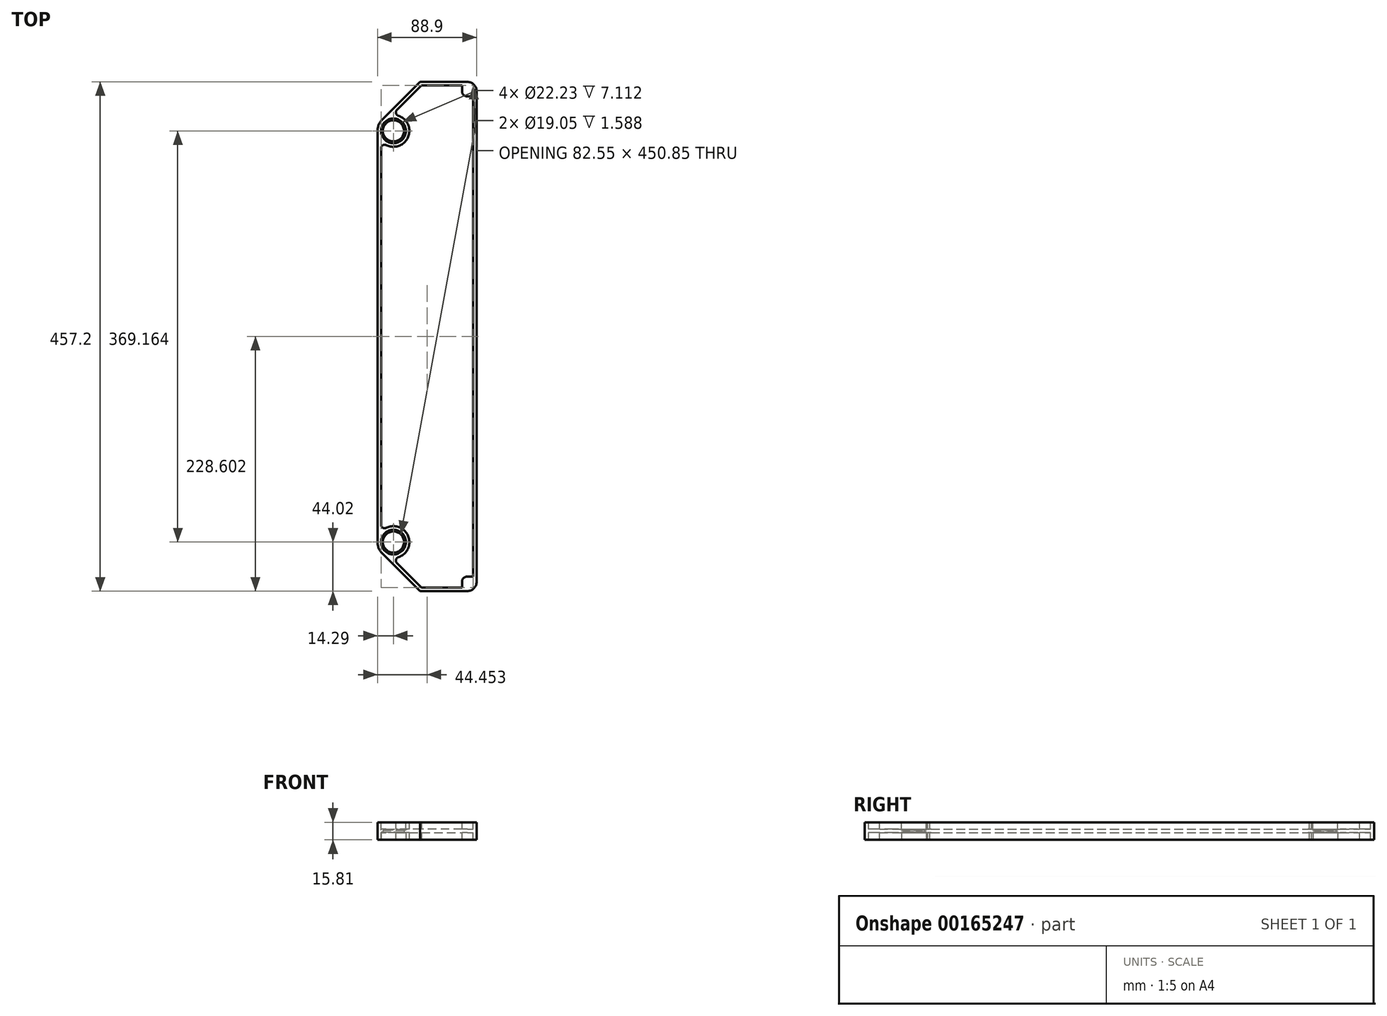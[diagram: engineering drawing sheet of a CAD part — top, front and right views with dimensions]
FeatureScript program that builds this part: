
annotation { "Feature Type Name" : "Feature", "Feature Type Description" : "" }
export const myFeature = defineFeature(function(context is Context, id is Id, definition is map)
    precondition{}
    {
        {
            var Q0;
            Q0=qCreatedBy(makeId("Top.planeOp"),FACE);
            var sketch = newSketch(context, id + "F0", { "sketchPlane" : qUnion([Q0])});
            skCircle(sketch, "E0", {"center": v(0, 0) * mm, "radius": 9.53 * mm});
            skArc(sketch, "E1", {"start": v(-14.29, 0) * mm, "mid": v(-13.2, -5.47) * mm, "end": v(-10.1, -10.1) * mm});
            skLineSegment(sketch, "E2", {"start": v(-14.29, 0) * mm, "end": v(-14.29, 369.16) * mm});
            skArc(sketch, "E3", {"start": v(-10.1, 379.27) * mm, "mid": v(-13.2, 374.63) * mm, "end": v(-14.29, 369.16) * mm});
            skCircle(sketch, "E4", {"center": v(0, 369.16) * mm, "radius": 9.53 * mm});
            skLineSegment(sketch, "E5", {"start": v(-10.1, -10.1) * mm, "end": v(23.81, -44.02) * mm});
            skLineSegment(sketch, "E6", {"start": v(23.81, -44.02) * mm, "end": v(74.61, -44.02) * mm});
            skLineSegment(sketch, "E7", {"start": v(74.61, -44.02) * mm, "end": v(74.61, 413.18) * mm});
            skLineSegment(sketch, "E8", {"start": v(74.61, 413.18) * mm, "end": v(23.81, 413.18) * mm});
            skLineSegment(sketch, "E9", {"start": v(23.81, 413.18) * mm, "end": v(-10.1, 379.27) * mm});
            skLineSegment(sketch, "E10", {"start": v(-14.29, 184.58) * mm, "end": v(23.81, 184.58) * mm, "construction": true});
            skLineSegment(sketch, "E11", {"start": v(23.81, -44.02) * mm, "end": v(23.81, 413.18) * mm, "construction": true});
            skSolve(sketch);
        }
        {
            var Q0;
            Q0=qSketchRegion(id+"F0",true);
            extrude(context, id + "F1", {"entities" : qUnion([Q0]), "depth" : 15.8 * mm});
        }
        {
            var Q0;
            Q0=makeQuery(id+"F1.opExtrude","CAP_FACE",FACE,{"disambiguationData":[OSD([sQuery(id+"F0.wireOp",EDGE,"E0"),sQuery(id+"F0.wireOp",EDGE,"E1"),sQuery(id+"F0.wireOp",EDGE,"E2"),sQuery(id+"F0.wireOp",EDGE,"E3"),sQuery(id+"F0.wireOp",EDGE,"E4"),sQuery(id+"F0.wireOp",EDGE,"E5"),sQuery(id+"F0.wireOp",EDGE,"E6"),sQuery(id+"F0.wireOp",EDGE,"E7"),sQuery(id+"F0.wireOp",EDGE,"E8"),sQuery(id+"F0.wireOp",EDGE,"E9")])],"isStart":false});
            var sketch = newSketch(context, id + "F2", { "sketchPlane" : qUnion([Q0])});
            skCircle(sketch, "E12", {"center": v(0, 369.16) * mm, "radius": 11.11 * mm});
            skCircle(sketch, "E13", {"center": v(0, 0) * mm, "radius": 11.11 * mm});
            skSolve(sketch);
        }
        {
            var Q0;
            Q0=qSketchRegion(id+"F2",true);
            extrude(context, id + "F3", {"entities" : qUnion([Q0]), "operationType" : NewBodyOperationType.REMOVE, "oppositeDirection" : true, "depth" : 7.11 * mm});
        }
        {
            var Q0;
            Q0=makeQuery(id+"F1.opExtrude","CAP_FACE",FACE,{"disambiguationData":[OSD([sQuery(id+"F0.wireOp",EDGE,"E0"),sQuery(id+"F0.wireOp",EDGE,"E1"),sQuery(id+"F0.wireOp",EDGE,"E2"),sQuery(id+"F0.wireOp",EDGE,"E3"),sQuery(id+"F0.wireOp",EDGE,"E4"),sQuery(id+"F0.wireOp",EDGE,"E5"),sQuery(id+"F0.wireOp",EDGE,"E6"),sQuery(id+"F0.wireOp",EDGE,"E7"),sQuery(id+"F0.wireOp",EDGE,"E8"),sQuery(id+"F0.wireOp",EDGE,"E9")])],"isStart":true});
            var sketch = newSketch(context, id + "F4", { "sketchPlane" : qUnion([Q0])});
            skCircle(sketch, "E14", {"center": v(0, 0) * mm, "radius": 11.11 * mm});
            skCircle(sketch, "E15", {"center": v(0, -369.16) * mm, "radius": 11.11 * mm});
            skSolve(sketch);
        }
        {
            var Q0;
            Q0 = qSketchRegion(id + "F4", true);
            extrude(context, id + "F5", {"entities" : qUnion([Q0]), "operationType" : NewBodyOperationType.REMOVE, "oppositeDirection" : true, "depth" : 7.11 * mm});
        }
        {
            var Q0;
            Q0=makeQuery(id+"F1.opExtrude","CAP_FACE",FACE,{"disambiguationData":[OSD([sQuery(id+"F0.wireOp",EDGE,"E0"),sQuery(id+"F0.wireOp",EDGE,"E1"),sQuery(id+"F0.wireOp",EDGE,"E2"),sQuery(id+"F0.wireOp",EDGE,"E3"),sQuery(id+"F0.wireOp",EDGE,"E4"),sQuery(id+"F0.wireOp",EDGE,"E5"),sQuery(id+"F0.wireOp",EDGE,"E6"),sQuery(id+"F0.wireOp",EDGE,"E7"),sQuery(id+"F0.wireOp",EDGE,"E8"),sQuery(id+"F0.wireOp",EDGE,"E9")])],"isStart":true});
            shell(context, id + "F6", {"entities" : qUnion([Q0]), "thickness" : 3.17 * mm});
        }
        {
            var Q0;
            {var subQ0=sQuery(id+"F4.wireOp",EDGE,"E15");var subQ1=sQuery(id+"F2.wireOp",EDGE,"E12");var subQ2=sQuery(id+"F0.wireOp",EDGE,"E9");var subQ3=sQuery(id+"F0.wireOp",EDGE,"E8");var subQ4=sQuery(id+"F0.wireOp",EDGE,"E7");var subQ5=sQuery(id+"F0.wireOp",EDGE,"E6");var subQ6=sQuery(id+"F0.wireOp",EDGE,"E5");var subQ7=sQuery(id+"F0.wireOp",EDGE,"E4");var subQ8=sQuery(id+"F0.wireOp",EDGE,"E3");var subQ9=sQuery(id+"F0.wireOp",EDGE,"E2");var subQ10=sQuery(id+"F0.wireOp",EDGE,"E1");var subQ11=sQuery(id+"F0.wireOp",EDGE,"E0");var subQ12=makeQuery(id+"F1.opExtrude","CAP_FACE",FACE,{"disambiguationData":[OSD([subQ11,subQ10,subQ9,subQ8,subQ7,subQ6,subQ5,subQ4,subQ3,subQ2])],"isStart":false});var subQ13=makeQuery(id+"F5.boolean.opBoolean","COPY",FACE,{"derivedFrom":makeQuery(id+"F5.opExtrude","SWEPT_FACE",FACE,{"disambiguationData":[OSD([subQ0])]})});var subQ14=makeQuery(id+"F3.boolean.opBoolean","COPY",FACE,{"derivedFrom":makeQuery(id+"F3.opExtrude","SWEPT_FACE",FACE,{"disambiguationData":[OSD([subQ1])]})});var subQ15=makeQuery(id+"F1.opExtrude","SWEPT_FACE",FACE,{"disambiguationData":[OSD([subQ2])]});Q0=makeQuery(id+"F11.boolean.opBoolean","SPLIT",EDGE,{"disambiguationData":[TD([subQ12])],"derivedFrom":makeQuery(id+"F8.boolean.opBoolean","MERGE",EDGE,{"derivedFrom":[makeQuery(id+"F6.opShell","TWEAK_EDGE",EDGE,{"derivedFrom":[subQ15,subQ14,subQ13]}),makeQuery(id+"F8.opExtrude","SWEPT_EDGE",EDGE,{"disambiguationData":[OSD([subQ11,subQ10,subQ9,subQ8,subQ7,subQ6,subQ5,subQ4,subQ3,subQ2,subQ1,subQ0]),TDD([makeQuery(id+"F6.opShell","TWEAK_VERTEX",VERTEX,{"derivedFrom":[subQ15,subQ14,subQ12,subQ13]})])]})]})});}
            var Q1;
            {var subQ0=sQuery(id+"F4.wireOp",EDGE,"E15");var subQ1=sQuery(id+"F2.wireOp",EDGE,"E12");var subQ2=sQuery(id+"F0.wireOp",EDGE,"E2");var subQ3=sQuery(id+"F0.wireOp",EDGE,"E9");var subQ4=sQuery(id+"F0.wireOp",EDGE,"E8");var subQ5=sQuery(id+"F0.wireOp",EDGE,"E7");var subQ6=sQuery(id+"F0.wireOp",EDGE,"E6");var subQ7=sQuery(id+"F0.wireOp",EDGE,"E5");var subQ8=sQuery(id+"F0.wireOp",EDGE,"E4");var subQ9=sQuery(id+"F0.wireOp",EDGE,"E3");var subQ10=sQuery(id+"F0.wireOp",EDGE,"E1");var subQ11=sQuery(id+"F0.wireOp",EDGE,"E0");var subQ12=makeQuery(id+"F1.opExtrude","CAP_FACE",FACE,{"disambiguationData":[OSD([subQ11,subQ10,subQ2,subQ9,subQ8,subQ7,subQ6,subQ5,subQ4,subQ3])],"isStart":false});var subQ13=makeQuery(id+"F5.boolean.opBoolean","COPY",FACE,{"derivedFrom":makeQuery(id+"F5.opExtrude","SWEPT_FACE",FACE,{"disambiguationData":[OSD([subQ0])]})});var subQ14=makeQuery(id+"F3.boolean.opBoolean","COPY",FACE,{"derivedFrom":makeQuery(id+"F3.opExtrude","SWEPT_FACE",FACE,{"disambiguationData":[OSD([subQ1])]})});var subQ15=makeQuery(id+"F1.opExtrude","SWEPT_FACE",FACE,{"disambiguationData":[OSD([subQ2])]});Q1=makeQuery(id+"F11.boolean.opBoolean","SPLIT",EDGE,{"disambiguationData":[TD([subQ12])],"derivedFrom":makeQuery(id+"F8.boolean.opBoolean","MERGE",EDGE,{"derivedFrom":[makeQuery(id+"F6.opShell","TWEAK_EDGE",EDGE,{"derivedFrom":[subQ15,subQ14,subQ13]}),makeQuery(id+"F8.opExtrude","SWEPT_EDGE",EDGE,{"disambiguationData":[OSD([subQ11,subQ10,subQ2,subQ9,subQ8,subQ7,subQ6,subQ5,subQ4,subQ3,subQ1,subQ0]),TDD([makeQuery(id+"F6.opShell","TWEAK_VERTEX",VERTEX,{"derivedFrom":[subQ15,subQ14,subQ12,subQ13]})])]})]})});}
            var Q2;
            {var subQ0=sQuery(id+"F4.wireOp",EDGE,"E14");var subQ1=sQuery(id+"F2.wireOp",EDGE,"E13");var subQ2=sQuery(id+"F0.wireOp",EDGE,"E9");var subQ3=sQuery(id+"F0.wireOp",EDGE,"E8");var subQ4=sQuery(id+"F0.wireOp",EDGE,"E7");var subQ5=sQuery(id+"F0.wireOp",EDGE,"E6");var subQ6=sQuery(id+"F0.wireOp",EDGE,"E5");var subQ7=sQuery(id+"F0.wireOp",EDGE,"E4");var subQ8=sQuery(id+"F0.wireOp",EDGE,"E3");var subQ9=sQuery(id+"F0.wireOp",EDGE,"E2");var subQ10=sQuery(id+"F0.wireOp",EDGE,"E1");var subQ11=sQuery(id+"F0.wireOp",EDGE,"E0");var subQ12=makeQuery(id+"F1.opExtrude","CAP_FACE",FACE,{"disambiguationData":[OSD([subQ11,subQ10,subQ9,subQ8,subQ7,subQ6,subQ5,subQ4,subQ3,subQ2])],"isStart":false});var subQ13=makeQuery(id+"F5.boolean.opBoolean","COPY",FACE,{"derivedFrom":makeQuery(id+"F5.opExtrude","SWEPT_FACE",FACE,{"disambiguationData":[OSD([subQ0])]})});var subQ14=makeQuery(id+"F3.boolean.opBoolean","COPY",FACE,{"derivedFrom":makeQuery(id+"F3.opExtrude","SWEPT_FACE",FACE,{"disambiguationData":[OSD([subQ1])]})});var subQ15=makeQuery(id+"F1.opExtrude","SWEPT_FACE",FACE,{"disambiguationData":[OSD([subQ6])]});Q2=makeQuery(id+"F11.boolean.opBoolean","SPLIT",EDGE,{"disambiguationData":[TD([subQ12])],"derivedFrom":makeQuery(id+"F8.boolean.opBoolean","MERGE",EDGE,{"derivedFrom":[makeQuery(id+"F6.opShell","TWEAK_EDGE",EDGE,{"derivedFrom":[subQ15,subQ14,subQ13]}),makeQuery(id+"F8.opExtrude","SWEPT_EDGE",EDGE,{"disambiguationData":[OSD([subQ11,subQ10,subQ9,subQ8,subQ7,subQ6,subQ5,subQ4,subQ3,subQ2,subQ1,subQ0]),TDD([makeQuery(id+"F6.opShell","TWEAK_VERTEX",VERTEX,{"derivedFrom":[subQ15,subQ14,subQ12,subQ13]})])]})]})});}
            var Q3;
            {var subQ0=sQuery(id+"F4.wireOp",EDGE,"E14");var subQ1=sQuery(id+"F2.wireOp",EDGE,"E13");var subQ2=sQuery(id+"F0.wireOp",EDGE,"E9");var subQ3=sQuery(id+"F0.wireOp",EDGE,"E8");var subQ4=sQuery(id+"F0.wireOp",EDGE,"E7");var subQ5=sQuery(id+"F0.wireOp",EDGE,"E6");var subQ6=sQuery(id+"F0.wireOp",EDGE,"E5");var subQ7=sQuery(id+"F0.wireOp",EDGE,"E4");var subQ8=sQuery(id+"F0.wireOp",EDGE,"E3");var subQ9=sQuery(id+"F0.wireOp",EDGE,"E2");var subQ10=sQuery(id+"F0.wireOp",EDGE,"E1");var subQ11=sQuery(id+"F0.wireOp",EDGE,"E0");var subQ12=makeQuery(id+"F1.opExtrude","CAP_FACE",FACE,{"disambiguationData":[OSD([subQ11,subQ10,subQ9,subQ8,subQ7,subQ6,subQ5,subQ4,subQ3,subQ2])],"isStart":false});var subQ13=makeQuery(id+"F5.boolean.opBoolean","COPY",FACE,{"derivedFrom":makeQuery(id+"F5.opExtrude","SWEPT_FACE",FACE,{"disambiguationData":[OSD([subQ0])]})});var subQ14=makeQuery(id+"F3.boolean.opBoolean","COPY",FACE,{"derivedFrom":makeQuery(id+"F3.opExtrude","SWEPT_FACE",FACE,{"disambiguationData":[OSD([subQ1])]})});var subQ15=makeQuery(id+"F1.opExtrude","SWEPT_FACE",FACE,{"disambiguationData":[OSD([subQ9])]});Q3=makeQuery(id+"F11.boolean.opBoolean","SPLIT",EDGE,{"disambiguationData":[TD([subQ12])],"derivedFrom":makeQuery(id+"F8.boolean.opBoolean","MERGE",EDGE,{"derivedFrom":[makeQuery(id+"F6.opShell","TWEAK_EDGE",EDGE,{"derivedFrom":[subQ15,subQ14,subQ13]}),makeQuery(id+"F8.opExtrude","SWEPT_EDGE",EDGE,{"disambiguationData":[OSD([subQ11,subQ10,subQ9,subQ8,subQ7,subQ6,subQ5,subQ4,subQ3,subQ2,subQ1,subQ0]),TDD([makeQuery(id+"F6.opShell","TWEAK_VERTEX",VERTEX,{"derivedFrom":[subQ15,subQ14,subQ12,subQ13]})])]})]})});}
            fillet(context, id + "F7", {"entities" : qUnion([Q0, Q1, Q2, Q3]), "radius" : 3.17 * mm, "tangentPropagation" : true, "allowEdgeOverflow" : false});
        }
        {
            var Q0;
            Q0=makeQuery(id+"F6.opShell","OFFSET_FACE",FACE,{"disambiguationData":[OSD([sQuery(id+"F0.wireOp",EDGE,"E0"),sQuery(id+"F0.wireOp",EDGE,"E1"),sQuery(id+"F0.wireOp",EDGE,"E2"),sQuery(id+"F0.wireOp",EDGE,"E3"),sQuery(id+"F0.wireOp",EDGE,"E4"),sQuery(id+"F0.wireOp",EDGE,"E5"),sQuery(id+"F0.wireOp",EDGE,"E6"),sQuery(id+"F0.wireOp",EDGE,"E7"),sQuery(id+"F0.wireOp",EDGE,"E8"),sQuery(id+"F0.wireOp",EDGE,"E9")])]});
            var Q1;
            Q1=makeQuery(id+"F1.opExtrude","CAP_FACE",FACE,{"disambiguationData":[OSD([sQuery(id+"F0.wireOp",EDGE,"E0"),sQuery(id+"F0.wireOp",EDGE,"E1"),sQuery(id+"F0.wireOp",EDGE,"E2"),sQuery(id+"F0.wireOp",EDGE,"E3"),sQuery(id+"F0.wireOp",EDGE,"E4"),sQuery(id+"F0.wireOp",EDGE,"E5"),sQuery(id+"F0.wireOp",EDGE,"E6"),sQuery(id+"F0.wireOp",EDGE,"E7"),sQuery(id+"F0.wireOp",EDGE,"E8"),sQuery(id+"F0.wireOp",EDGE,"E9")])],"isStart":false});
            extrude(context, id + "F8", {"entities" : qUnion([Q0]), "operationType" : NewBodyOperationType.REMOVE, "endBound" : BoundingType.UP_TO_SURFACE, "oppositeDirection" : true, "endBoundEntityFace" : qUnion([Q1]), "depth" : 25.4 * mm});
        }
        {
            var Q0;
            Q0=makeQuery(id+"F1.opExtrude","CAP_FACE",FACE,{"disambiguationData":[OSD([sQuery(id+"F0.wireOp",EDGE,"E0"),sQuery(id+"F0.wireOp",EDGE,"E1"),sQuery(id+"F0.wireOp",EDGE,"E2"),sQuery(id+"F0.wireOp",EDGE,"E3"),sQuery(id+"F0.wireOp",EDGE,"E4"),sQuery(id+"F0.wireOp",EDGE,"E5"),sQuery(id+"F0.wireOp",EDGE,"E6"),sQuery(id+"F0.wireOp",EDGE,"E7"),sQuery(id+"F0.wireOp",EDGE,"E8"),sQuery(id+"F0.wireOp",EDGE,"E9")])],"isStart":false});
            cPlane(context, id + "F9", {"entities" : qUnion([Q0]), "cplaneType" : CPlaneType.OFFSET, "offset" : 7.9 * mm, "oppositeDirection" : true, "width" : 152.4 * mm, "height" : 152.4 * mm});
        }
        {
            var Q0;
            Q0=qCreatedBy(id+"F9.planeOp",FACE);
            var sketch = newSketch(context, id + "F10", { "sketchPlane" : qUnion([Q0])});
            skLineSegment(sketch, "E16.bottom", {"start": v(74.61, 413.18) * mm, "end": v(-14.29, 413.18) * mm});
            skLineSegment(sketch, "E16.top", {"start": v(74.61, -44.02) * mm, "end": v(-14.29, -44.02) * mm});
            skLineSegment(sketch, "E16.left", {"start": v(74.61, 413.18) * mm, "end": v(74.61, -44.02) * mm});
            skLineSegment(sketch, "E16.right", {"start": v(-14.29, 413.18) * mm, "end": v(-14.29, -44.02) * mm});
            skCircle(sketch, "E17", {"center": v(0, 0) * mm, "radius": 11.11 * mm});
            skCircle(sketch, "E18", {"center": v(0, 369.16) * mm, "radius": 11.11 * mm});
            skLineSegment(sketch, "E19", {"start": v(-10.1, 379.27) * mm, "end": v(23.81, 413.18) * mm});
            skArc(sketch, "E20", {"start": v(-10.1, 379.27) * mm, "mid": v(-13.2, 374.63) * mm, "end": v(-14.29, 369.16) * mm});
            skLineSegment(sketch, "E21", {"start": v(23.81, -44.02) * mm, "end": v(-10.1, -10.1) * mm});
            skArc(sketch, "E22", {"start": v(-14.29, 0) * mm, "mid": v(-13.2, -5.47) * mm, "end": v(-10.1, -10.1) * mm});
            skSolve(sketch);
        }
        {
            var Q0;
            {var subQ3=sQuery(id+"F10.wireOp",EDGE,"E16.left");Q0=makeQuery(id+"F10.imprint","IMPRINT",FACE,{"disambiguationData":[TD([[makeQuery(id+"F10.imprint","IMPRINT",EDGE,{"derivedFrom":subQ3}),-1.0]])]});}
            extrude(context, id + "F11", {"entities" : qUnion([Q0]), "operationType" : NewBodyOperationType.ADD, "endBound" : BoundingType.SYMMETRIC, "depth" : 3.17 * mm});
        }
        {
            var Q0;
            Q0=makeQuery(id+"F1.opExtrude","CAP_FACE",FACE,{"disambiguationData":[OSD([sQuery(id+"F0.wireOp",EDGE,"E0"),sQuery(id+"F0.wireOp",EDGE,"E1"),sQuery(id+"F0.wireOp",EDGE,"E2"),sQuery(id+"F0.wireOp",EDGE,"E3"),sQuery(id+"F0.wireOp",EDGE,"E4"),sQuery(id+"F0.wireOp",EDGE,"E5"),sQuery(id+"F0.wireOp",EDGE,"E6"),sQuery(id+"F0.wireOp",EDGE,"E7"),sQuery(id+"F0.wireOp",EDGE,"E8"),sQuery(id+"F0.wireOp",EDGE,"E9")])],"isStart":true});
            var sketch = newSketch(context, id + "F12", { "sketchPlane" : qUnion([Q0])});
            skLineSegment(sketch, "E23.bottom", {"start": v(74.61, -413.18) * mm, "end": v(61.52, -413.18) * mm});
            skLineSegment(sketch, "E23.top", {"start": v(74.61, -400.09) * mm, "end": v(61.52, -400.09) * mm});
            skLineSegment(sketch, "E23.left", {"start": v(74.61, -413.18) * mm, "end": v(74.61, -400.09) * mm});
            skLineSegment(sketch, "E23.right", {"start": v(61.52, -413.18) * mm, "end": v(61.52, -400.09) * mm});
            skLineSegment(sketch, "E24.bottom", {"start": v(74.61, 44.02) * mm, "end": v(61.52, 44.02) * mm});
            skLineSegment(sketch, "E24.top", {"start": v(74.61, 30.92) * mm, "end": v(61.52, 30.92) * mm});
            skLineSegment(sketch, "E24.left", {"start": v(74.61, 44.02) * mm, "end": v(74.61, 30.92) * mm});
            skLineSegment(sketch, "E24.right", {"start": v(61.52, 44.02) * mm, "end": v(61.52, 30.92) * mm});
            skSolve(sketch);
        }
        {
            var Q0;
            Q0 = qSketchRegion(id + "F12", true);
            var Q1;
            Q1=makeQuery(id+"F1.opExtrude","CAP_FACE",FACE,{"disambiguationData":[OSD([sQuery(id+"F0.wireOp",EDGE,"E0"),sQuery(id+"F0.wireOp",EDGE,"E1"),sQuery(id+"F0.wireOp",EDGE,"E2"),sQuery(id+"F0.wireOp",EDGE,"E3"),sQuery(id+"F0.wireOp",EDGE,"E4"),sQuery(id+"F0.wireOp",EDGE,"E5"),sQuery(id+"F0.wireOp",EDGE,"E6"),sQuery(id+"F0.wireOp",EDGE,"E7"),sQuery(id+"F0.wireOp",EDGE,"E8"),sQuery(id+"F0.wireOp",EDGE,"E9")])],"isStart":false});
            extrude(context, id + "F13", {"entities" : qUnion([Q0]), "operationType" : NewBodyOperationType.ADD, "endBound" : BoundingType.UP_TO_SURFACE, "oppositeDirection" : true, "endBoundEntityFace" : qUnion([Q1]), "depth" : 25.4 * mm});
        }
        {
            var Q0;
            {var subQ0=sQuery(id+"F12.wireOp",EDGE,"E23.top");var subQ1=sQuery(id+"F12.wireOp",EDGE,"E23.right");Q0=makeQuery(id+"F13.boolean.opBoolean","SPLIT",EDGE,{"disambiguationData":[TD([makeQuery(id+"F13.opExtrude","CAP_FACE",FACE,{"disambiguationData":[OSD([sQuery(id+"F12.wireOp",EDGE,"E23.bottom"),subQ0,sQuery(id+"F12.wireOp",EDGE,"E23.left"),subQ1])],"isStart":false})])],"derivedFrom":makeQuery(id+"F13.opExtrude","SWEPT_EDGE",EDGE,{"disambiguationData":[OSD([subQ0,subQ1])]})});}
            var Q1;
            {var subQ0=sQuery(id+"F12.wireOp",EDGE,"E23.top");var subQ1=sQuery(id+"F12.wireOp",EDGE,"E23.right");Q1=makeQuery(id+"F13.boolean.opBoolean","SPLIT",EDGE,{"disambiguationData":[TD([makeQuery(id+"F13.opExtrude","CAP_FACE",FACE,{"disambiguationData":[OSD([sQuery(id+"F12.wireOp",EDGE,"E23.bottom"),subQ0,sQuery(id+"F12.wireOp",EDGE,"E23.left"),subQ1])],"isStart":true})])],"derivedFrom":makeQuery(id+"F13.opExtrude","SWEPT_EDGE",EDGE,{"disambiguationData":[OSD([subQ0,subQ1])]})});}
            var Q2;
            {var subQ0=sQuery(id+"F12.wireOp",EDGE,"E24.right");var subQ1=sQuery(id+"F12.wireOp",EDGE,"E24.top");Q2=makeQuery(id+"F13.boolean.opBoolean","SPLIT",EDGE,{"disambiguationData":[TD([makeQuery(id+"F13.opExtrude","CAP_FACE",FACE,{"disambiguationData":[OSD([sQuery(id+"F12.wireOp",EDGE,"E23.bottom"),sQuery(id+"F12.wireOp",EDGE,"E23.top"),sQuery(id+"F12.wireOp",EDGE,"E23.left"),sQuery(id+"F12.wireOp",EDGE,"E23.right")])],"isStart":false})])],"derivedFrom":makeQuery(id+"F13.opExtrude","SWEPT_EDGE",EDGE,{"disambiguationData":[OSD([subQ1,subQ0])]})});}
            var Q3;
            {var subQ0=sQuery(id+"F12.wireOp",EDGE,"E24.right");var subQ1=sQuery(id+"F12.wireOp",EDGE,"E24.top");Q3=makeQuery(id+"F13.boolean.opBoolean","SPLIT",EDGE,{"disambiguationData":[TD([makeQuery(id+"F13.opExtrude","CAP_FACE",FACE,{"disambiguationData":[OSD([sQuery(id+"F12.wireOp",EDGE,"E23.bottom"),sQuery(id+"F12.wireOp",EDGE,"E23.top"),sQuery(id+"F12.wireOp",EDGE,"E23.left"),sQuery(id+"F12.wireOp",EDGE,"E23.right")])],"isStart":true})])],"derivedFrom":makeQuery(id+"F13.opExtrude","SWEPT_EDGE",EDGE,{"disambiguationData":[OSD([subQ1,subQ0])]})});}
            fillet(context, id + "F14", {"entities" : qUnion([Q0, Q1, Q2, Q3]), "radius" : 4.76 * mm, "tangentPropagation" : true, "allowEdgeOverflow" : false});
        }
        {
            var Q0;
            Q0=makeQuery(id+"F1.opExtrude","SWEPT_EDGE",EDGE,{"disambiguationData":[OSD([sQuery(id+"F0.wireOp",EDGE,"E6"),sQuery(id+"F0.wireOp",EDGE,"E7")])]});
            var Q1;
            Q1=makeQuery(id+"F1.opExtrude","SWEPT_EDGE",EDGE,{"disambiguationData":[OSD([sQuery(id+"F0.wireOp",EDGE,"E7"),sQuery(id+"F0.wireOp",EDGE,"E8")])]});
            fillet(context, id + "F15", {"entities" : qUnion([Q0, Q1]), "radius" : 8.33 * mm, "tangentPropagation" : true, "allowEdgeOverflow" : false});
        }
    });
